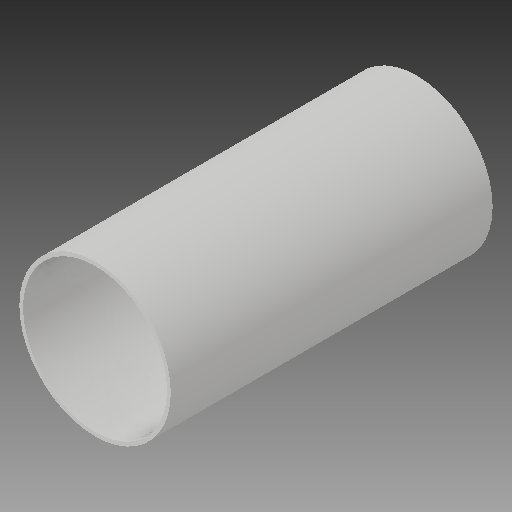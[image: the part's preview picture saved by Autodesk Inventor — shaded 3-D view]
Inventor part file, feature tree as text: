
AUTODESK INVENTOR PART (.ipt)
format: ipt  version: 2019 (Build 230136000, 136)  size: 102,912 bytes
history: native  units: mm
features: other x4, extrude x1, sketch x1, reference x1
ambient origin geometry x8: Origin, YZ Plane, XZ Plane, XY Plane, X Axis, Y Axis, Z Axis, Center Point
bodies: Body1 (feature_tree)
feature tree (7):
  other  "Твердое тело1"
  extrude  "Выдавливание1"  Depth=170.0mm TaperAngle=0.0deg
  sketch  "Эскиз1"
  reference  "Ссылка1"
  other  "<userpath>\Documents\GitHub\Tesla_coil_V1\3dModels\TeslaCoil.iam"
  other  "TeslaCoil.iam"
  other  "Cap:1"
